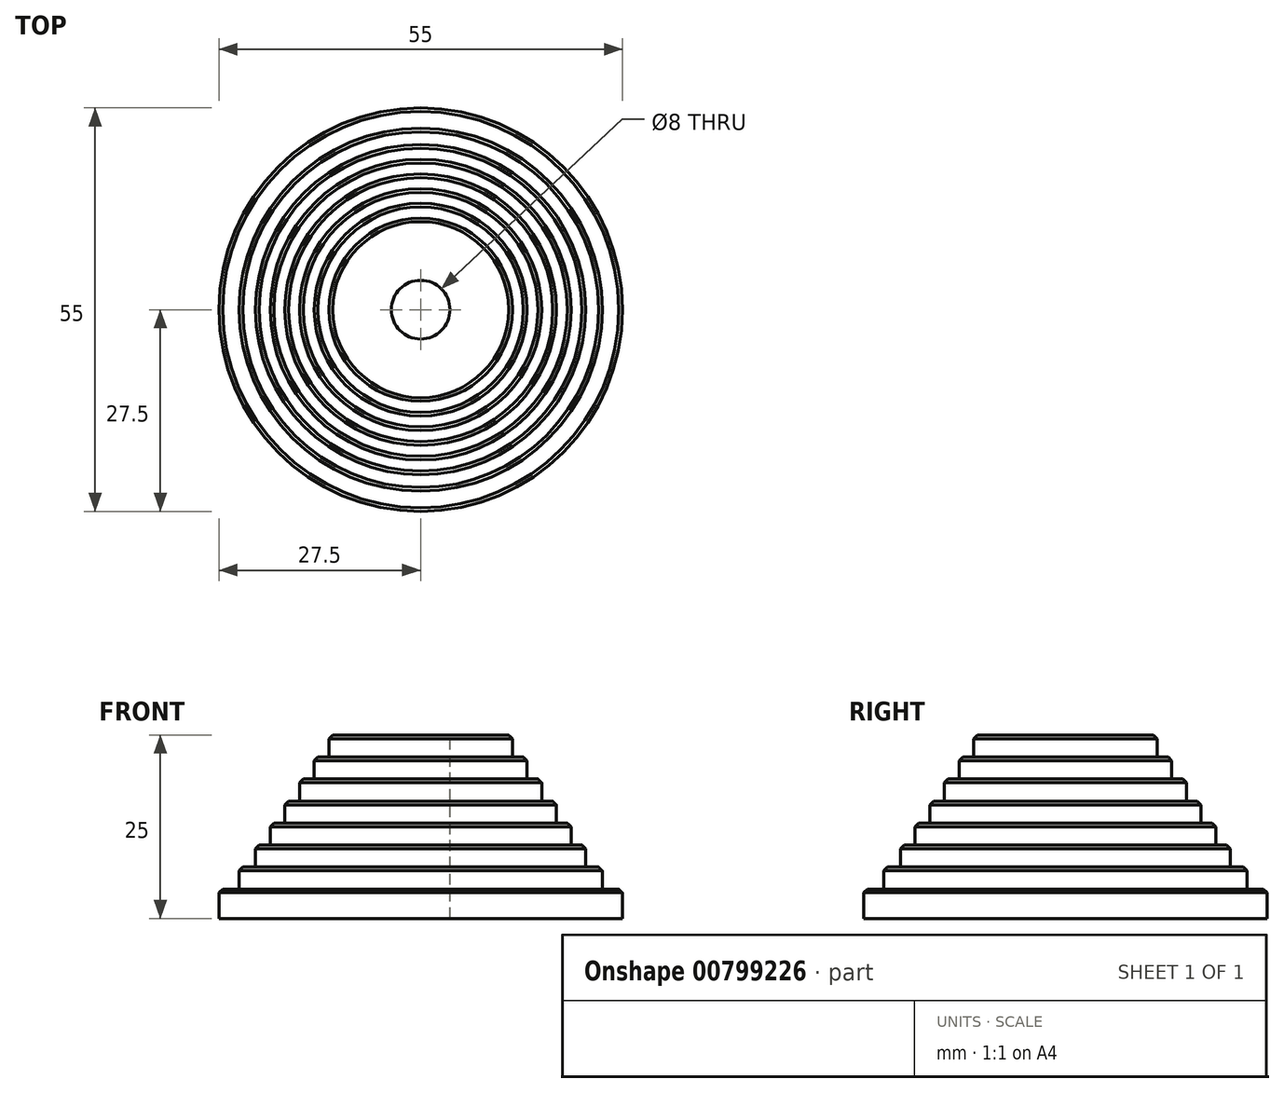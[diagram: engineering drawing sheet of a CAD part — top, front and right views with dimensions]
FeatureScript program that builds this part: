
annotation { "Feature Type Name" : "Feature", "Feature Type Description" : "" }
export const myFeature = defineFeature(function(context is Context, id is Id, definition is map)
    precondition{}
    {
        {
            var Q0;
            Q0=qCreatedBy(makeId("Top.planeOp"),FACE);
            var sketch = newSketch(context, id + "F0", { "sketchPlane" : qUnion([Q0])});
            skCircle(sketch, "E0.0", {"center": v(0, 0) * mm, "radius": 27.5 * mm});
            skSolve(sketch);
        }
        {
            var Q0;
            Q0 = qSketchRegion(id + "F0", true);
            extrude(context, id + "F1", {"entities" : qUnion([Q0]), "depth" : 4 * mm, "offsetDistance" : 25 * mm});
        }
        {
            var Q0;
            Q0=makeQuery(id+"F1.opExtrude","CAP_FACE",FACE,{"disambiguationData":[OSD([sQuery(id+"F0.wireOp",EDGE,"E0.0")])],"isStart":false});
            var sketch = newSketch(context, id + "F2", { "sketchPlane" : qUnion([Q0])});
            skCircle(sketch, "E1", {"center": v(0, 0) * mm, "radius": 24.75 * mm});
            skSolve(sketch);
        }
        {
            var Q0;
            Q0=makeQuery(id+"F2.imprint","IMPRINT",FACE,{"disambiguationData":[TD([[makeQuery(id+"F2.imprint","IMPRINT",EDGE,{"derivedFrom":sQuery(id+"F2.wireOp",EDGE,"E1")}),1.0]])]});
            extrude(context, id + "F3", {"entities" : qUnion([Q0]), "operationType" : NewBodyOperationType.ADD, "depth" : 3 * mm, "offsetDistance" : 25 * mm});
        }
        {
            var Q0;
            Q0=makeQuery(id+"F3.opExtrude","CAP_FACE",FACE,{"disambiguationData":[OSD([sQuery(id+"F2.wireOp",EDGE,"E1")])],"isStart":false});
            var sketch = newSketch(context, id + "F4", { "sketchPlane" : qUnion([Q0])});
            skCircle(sketch, "E2", {"center": v(0, 0) * mm, "radius": 22.5 * mm});
            skSolve(sketch);
        }
        {
            var Q0;
            Q0 = qSketchRegion(id + "F4", true);
            extrude(context, id + "F5", {"entities" : qUnion([Q0]), "operationType" : NewBodyOperationType.ADD, "depth" : 3 * mm, "offsetDistance" : 25 * mm});
        }
        {
            var Q0;
            Q0=makeQuery(id+"F5.opExtrude","CAP_FACE",FACE,{"disambiguationData":[OSD([sQuery(id+"F4.wireOp",EDGE,"E2")])],"isStart":false});
            var sketch = newSketch(context, id + "F6", { "sketchPlane" : qUnion([Q0])});
            skCircle(sketch, "E3", {"center": v(0, 0) * mm, "radius": 20.5 * mm});
            skSolve(sketch);
        }
        {
            var Q0;
            Q0=makeQuery(id+"F6.imprint","IMPRINT",FACE,{"disambiguationData":[TD([[makeQuery(id+"F6.imprint","IMPRINT",EDGE,{"derivedFrom":sQuery(id+"F6.wireOp",EDGE,"E3")}),1.0]])]});
            extrude(context, id + "F7", {"entities" : qUnion([Q0]), "operationType" : NewBodyOperationType.ADD, "depth" : 3 * mm, "offsetDistance" : 25 * mm});
        }
        {
            var Q0;
            Q0=makeQuery(id+"F7.opExtrude","CAP_FACE",FACE,{"disambiguationData":[OSD([sQuery(id+"F6.wireOp",EDGE,"E3")])],"isStart":false});
            var sketch = newSketch(context, id + "F8", { "sketchPlane" : qUnion([Q0])});
            skCircle(sketch, "E4", {"center": v(0, 0) * mm, "radius": 18.5 * mm});
            skSolve(sketch);
        }
        {
            var Q0;
            Q0=makeQuery(id+"F8.imprint","IMPRINT",FACE,{"disambiguationData":[TD([[makeQuery(id+"F8.imprint","IMPRINT",EDGE,{"derivedFrom":sQuery(id+"F8.wireOp",EDGE,"E4")}),1.0]])]});
            extrude(context, id + "F9", {"entities" : qUnion([Q0]), "operationType" : NewBodyOperationType.ADD, "depth" : 3 * mm, "offsetDistance" : 25 * mm});
        }
        {
            var Q0;
            Q0=makeQuery(id+"F9.opExtrude","CAP_FACE",FACE,{"disambiguationData":[OSD([sQuery(id+"F8.wireOp",EDGE,"E4")])],"isStart":false});
            var sketch = newSketch(context, id + "F10", { "sketchPlane" : qUnion([Q0])});
            skCircle(sketch, "E5", {"center": v(0, 0) * mm, "radius": 16.5 * mm});
            skSolve(sketch);
        }
        {
            var Q0;
            Q0 = qSketchRegion(id + "F10", true);
            extrude(context, id + "F11", {"entities" : qUnion([Q0]), "operationType" : NewBodyOperationType.ADD, "depth" : 3 * mm, "offsetDistance" : 25 * mm});
        }
        {
            var Q0;
            Q0=makeQuery(id+"F11.opExtrude","CAP_FACE",FACE,{"disambiguationData":[OSD([sQuery(id+"F10.wireOp",EDGE,"E5")])],"isStart":false});
            var sketch = newSketch(context, id + "F12", { "sketchPlane" : qUnion([Q0])});
            skCircle(sketch, "E6", {"center": v(0, 0) * mm, "radius": 14.5 * mm});
            skSolve(sketch);
        }
        {
            var Q0;
            Q0 = qSketchRegion(id + "F12", true);
            extrude(context, id + "F13", {"entities" : qUnion([Q0]), "operationType" : NewBodyOperationType.ADD, "depth" : 3 * mm, "offsetDistance" : 25 * mm});
        }
        {
            var Q0;
            Q0=makeQuery(id+"F13.opExtrude","CAP_FACE",FACE,{"disambiguationData":[OSD([sQuery(id+"F12.wireOp",EDGE,"E6")])],"isStart":false});
            var sketch = newSketch(context, id + "F14", { "sketchPlane" : qUnion([Q0])});
            skCircle(sketch, "E7", {"center": v(0, 0) * mm, "radius": 12.5 * mm});
            skSolve(sketch);
        }
        {
            var Q0;
            Q0 = qSketchRegion(id + "F14", true);
            extrude(context, id + "F15", {"entities" : qUnion([Q0]), "operationType" : NewBodyOperationType.ADD, "depth" : 3 * mm, "offsetDistance" : 25 * mm});
        }
        {
            var Q0;
            Q0=makeQuery(id+"F15.opExtrude","CAP_FACE",FACE,{"disambiguationData":[OSD([sQuery(id+"F14.wireOp",EDGE,"E7")])],"isStart":false});
            var sketch = newSketch(context, id + "F16", { "sketchPlane" : qUnion([Q0])});
            skCircle(sketch, "E8", {"center": v(0, 0) * mm, "radius": 4 * mm});
            skSolve(sketch);
        }
        {
            var Q0;
            Q0 = qSketchRegion(id + "F16", true);
            extrude(context, id + "F17", {"entities" : qUnion([Q0]), "operationType" : NewBodyOperationType.REMOVE, "oppositeDirection" : true, "depth" : 35 * mm, "offsetDistance" : 25 * mm});
        }
        {
            var Q0;
            Q0=makeQuery(id+"F15.opExtrude","CAP_EDGE",EDGE,{"disambiguationData":[OSD([sQuery(id+"F14.wireOp",EDGE,"E7")])],"isStart":false});
            chamfer(context, id + "F18", {"entities" : qUnion([Q0]), "width" : .5 * mm, "tangentPropagation" : true});
        }
        {
            var Q0;
            Q0=makeQuery(id+"F13.opExtrude","CAP_EDGE",EDGE,{"disambiguationData":[OSD([sQuery(id+"F12.wireOp",EDGE,"E6")])],"isStart":false});
            var Q1;
            Q1=makeQuery(id+"F11.opExtrude","CAP_EDGE",EDGE,{"disambiguationData":[OSD([sQuery(id+"F10.wireOp",EDGE,"E5")])],"isStart":false});
            var Q2;
            Q2=makeQuery(id+"F9.opExtrude","CAP_EDGE",EDGE,{"disambiguationData":[OSD([sQuery(id+"F8.wireOp",EDGE,"E4")])],"isStart":false});
            var Q3;
            Q3=makeQuery(id+"F7.opExtrude","CAP_EDGE",EDGE,{"disambiguationData":[OSD([sQuery(id+"F6.wireOp",EDGE,"E3")])],"isStart":false});
            var Q4;
            Q4=makeQuery(id+"F5.opExtrude","CAP_EDGE",EDGE,{"disambiguationData":[OSD([sQuery(id+"F4.wireOp",EDGE,"E2")])],"isStart":false});
            var Q5;
            Q5=makeQuery(id+"F3.opExtrude","CAP_EDGE",EDGE,{"disambiguationData":[OSD([sQuery(id+"F2.wireOp",EDGE,"E1")])],"isStart":false});
            var Q6;
            Q6=makeQuery(id+"F1.opExtrude","CAP_EDGE",EDGE,{"disambiguationData":[OSD([sQuery(id+"F0.wireOp",EDGE,"E0.0")])],"isStart":false});
            chamfer(context, id + "F19", {"entities" : qUnion([Q0, Q1, Q2, Q3, Q4, Q5, Q6]), "width" : .5 * mm, "tangentPropagation" : true});
        }
    });
